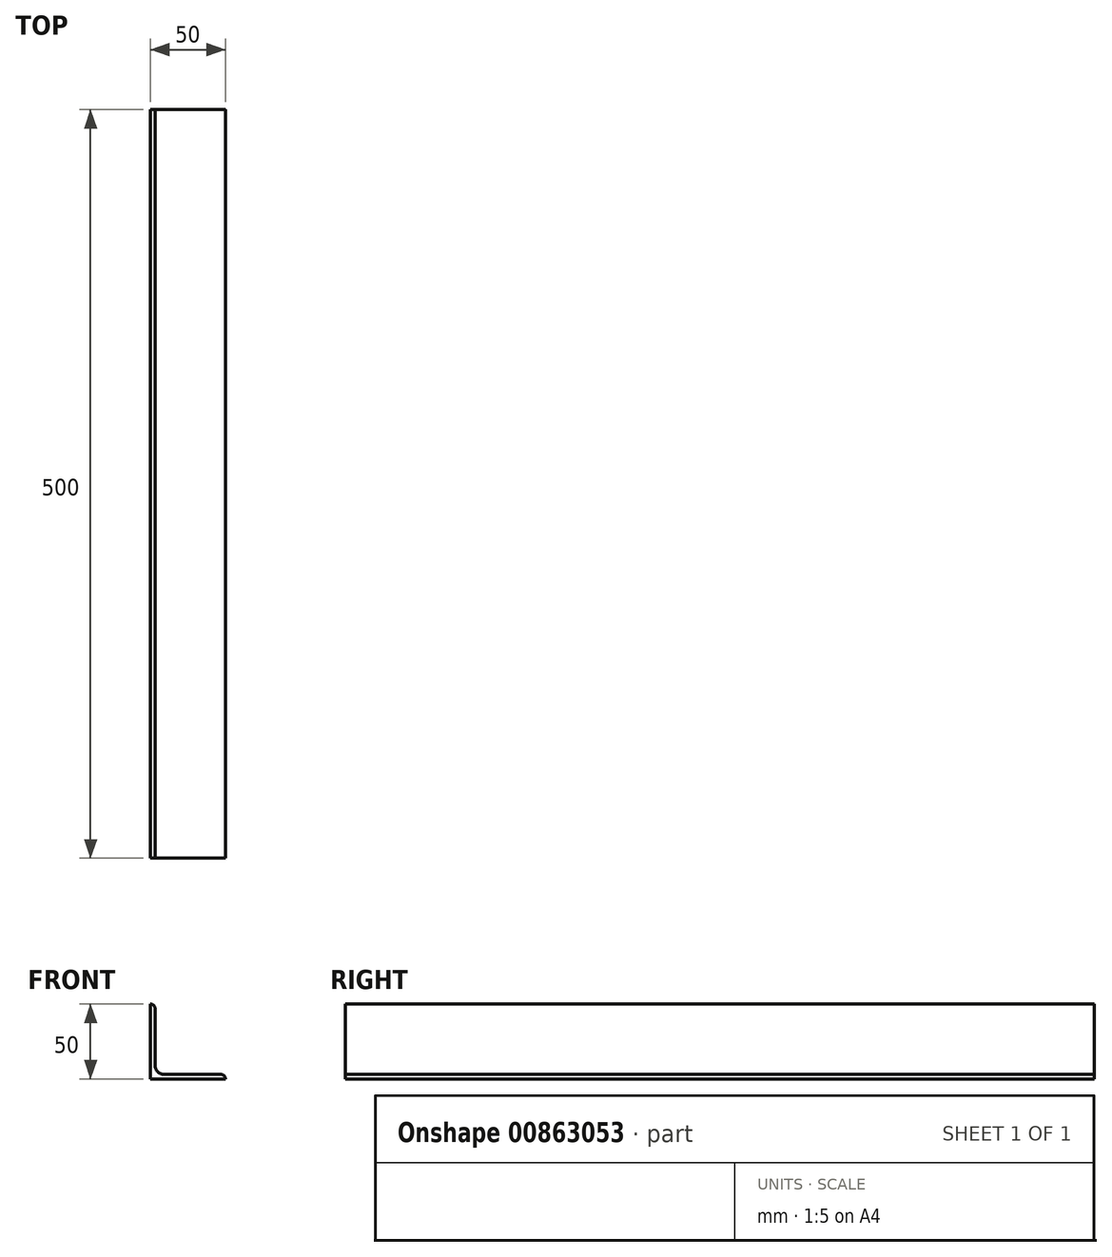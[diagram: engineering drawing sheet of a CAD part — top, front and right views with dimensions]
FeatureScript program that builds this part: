
annotation { "Feature Type Name" : "Feature", "Feature Type Description" : "" }
export const myFeature = defineFeature(function(context is Context, id is Id, definition is map)
    precondition{}
    {
        {
            var Q0;
            Q0=qCreatedBy(makeId("Front.planeOp"),FACE);
            var sketch = newSketch(context, id + "F0", { "sketchPlane" : qUnion([Q0])});
            skLineSegment(sketch, "E0", {"start": v(0, 0) * mm, "end": v(50, 0) * mm});
            skLineSegment(sketch, "E1", {"start": v(50, 0) * mm, "end": v(50, 0) * mm});
            skLineSegment(sketch, "E2", {"start": v(47, 3) * mm, "end": v(9, 3) * mm});
            skLineSegment(sketch, "E3", {"start": v(3, 9) * mm, "end": v(3, 47) * mm});
            skLineSegment(sketch, "E4", {"start": v(0, 50) * mm, "end": v(0, 50) * mm});
            skLineSegment(sketch, "E5", {"start": v(0, 50) * mm, "end": v(0, 0) * mm});
            skPoint(sketch, "E6.visualSharp", {"position": v(3, 3) * mm});
            skArc(sketch, "E6.filletArc", {"start": v(3, 9) * mm, "mid": v(4.76, 4.76) * mm, "end": v(9, 3) * mm});
            skPoint(sketch, "E7.visualSharp", {"position": v(3, 50) * mm});
            skArc(sketch, "E7.filletArc", {"start": v(3, 47) * mm, "mid": v(2.12, 49.12) * mm, "end": v(0, 50) * mm});
            skPoint(sketch, "E8.visualSharp", {"position": v(50, 3) * mm});
            skArc(sketch, "E8.filletArc", {"start": v(50, 0) * mm, "mid": v(49.12, 2.12) * mm, "end": v(47, 3) * mm});
            skSolve(sketch);
        }
        {
            var Q0;
            Q0=makeQuery(id+"F0.imprint","IMPRINT",FACE,{"disambiguationData":[TD([[makeQuery(id+"F0.imprint","IMPRINT",EDGE,{"derivedFrom":sQuery(id+"F0.wireOp",EDGE,"E0")}),1.0]])]});
            extrude(context, id + "F1", {"entities" : qUnion([Q0]), "oppositeDirection" : true, "depth" : 500 * mm, "offsetDistance" : 25 * mm});
        }
    });
